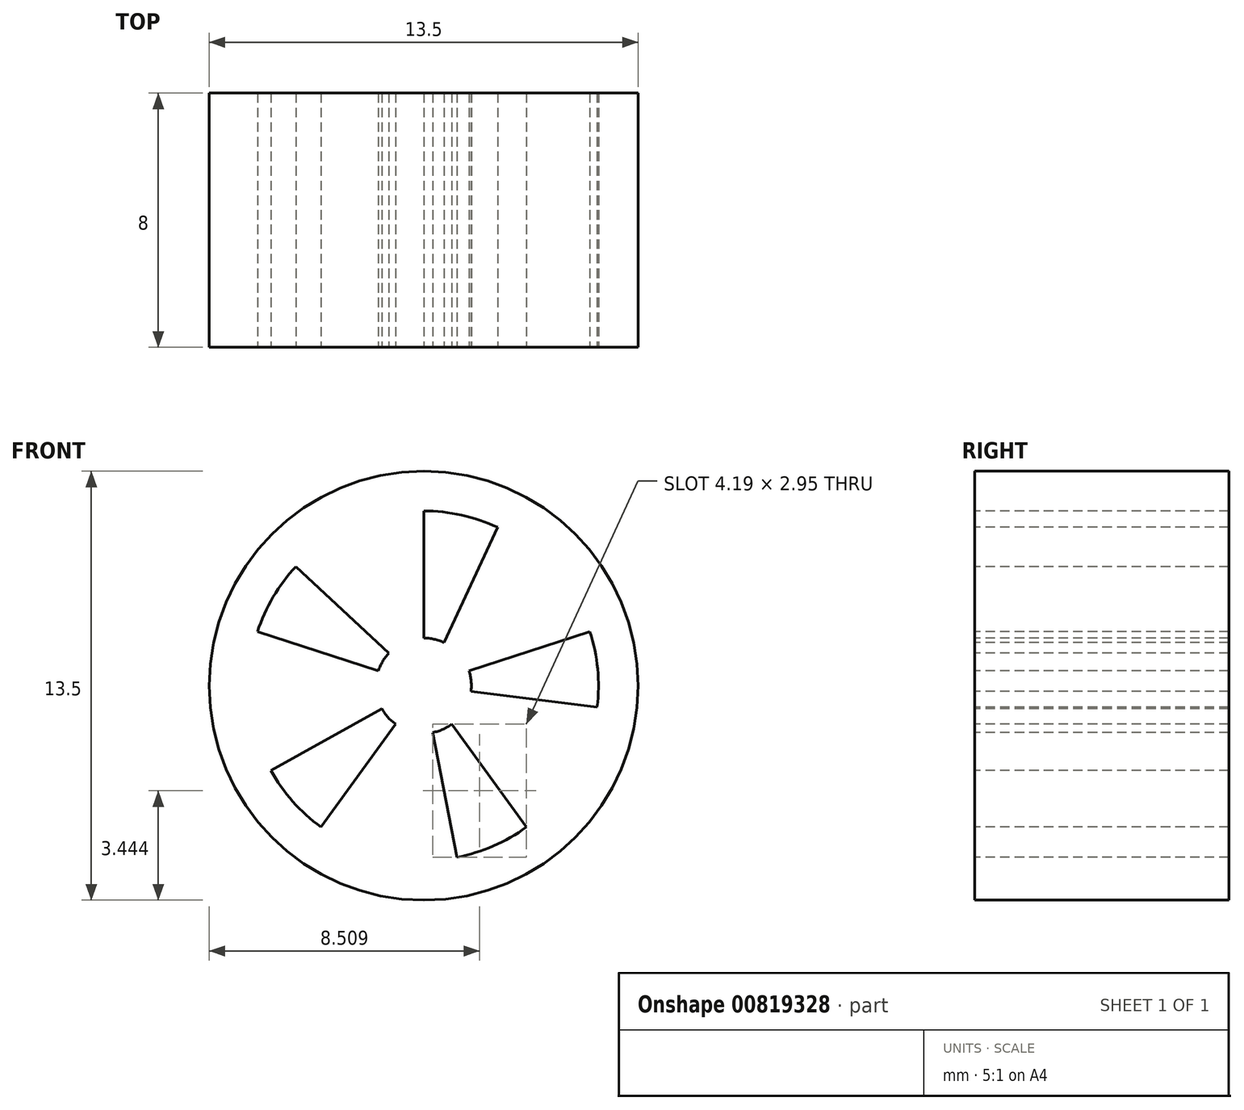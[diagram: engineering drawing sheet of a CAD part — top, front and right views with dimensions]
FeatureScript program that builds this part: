
annotation { "Feature Type Name" : "Feature", "Feature Type Description" : "" }
export const myFeature = defineFeature(function(context is Context, id is Id, definition is map)
    precondition{}
    {
        {
            var Q0;
            Q0=qCreatedBy(makeId("Front.planeOp"),FACE);
            var sketch = newSketch(context, id + "F0", { "sketchPlane" : qUnion([Q0])});
            skCircle(sketch, "E0", {"center": v(0, 0) * mm, "radius": 6.75 * mm});
            skSolve(sketch);
        }
        {
            var Q0;
            Q0=makeQuery(id+"F0.imprint","IMPRINT",FACE,{"disambiguationData":[TD([[makeQuery(id+"F0.imprint","IMPRINT",EDGE,{"derivedFrom":sQuery(id+"F0.wireOp",EDGE,"E0")}),1.0]])]});
            var Q1;
            Q1=sQuery(id+"F0.wireOp",EDGE,"E0");
            extrude(context, id + "F1", {"entities" : qUnion([Q0]), "surfaceEntities" : qUnion([Q1]), "depth" : 8 * mm, "offsetDistance" : 25 * mm});
        }
        {
            var Q0;
            Q0=makeQuery(id+"F1.opExtrude","CAP_FACE",FACE,{"disambiguationData":[OSD([sQuery(id+"F0.wireOp",EDGE,"E0")])],"isStart":false});
            var sketch = newSketch(context, id + "F2", { "sketchPlane" : qUnion([Q0])});
            skCircle(sketch, "E1", {"center": v(0, 0) * mm, "radius": 1.5 * mm});
            skCircle(sketch, "E2", {"center": v(0, 0) * mm, "radius": 5.5 * mm});
            skLineSegment(sketch, "E3", {"start": v(0, 1.5) * mm, "end": v(0, 5.5) * mm});
            skLineSegment(sketch, "E4", {"start": v(0.63, 1.36) * mm, "end": v(2.32, 4.98) * mm});
            skLineSegment(sketch, "E5.1.0", {"start": v(-1.43, 0.46) * mm, "end": v(-5.23, 1.7) * mm});
            skLineSegment(sketch, "E5.1.1", {"start": v(-1.1, 1.02) * mm, "end": v(-4.02, 3.75) * mm});
            skLineSegment(sketch, "E5.2.0", {"start": v(-0.88, -1.21) * mm, "end": v(-3.23, -4.45) * mm});
            skLineSegment(sketch, "E5.2.1", {"start": v(-1.31, -0.73) * mm, "end": v(-4.81, -2.67) * mm});
            skLineSegment(sketch, "E5.3.0", {"start": v(0.88, -1.21) * mm, "end": v(3.23, -4.45) * mm});
            skLineSegment(sketch, "E5.3.1", {"start": v(0.29, -1.47) * mm, "end": v(1.05, -5.4) * mm});
            skLineSegment(sketch, "E5.4.0", {"start": v(1.43, 0.46) * mm, "end": v(5.23, 1.7) * mm});
            skLineSegment(sketch, "E5.4.1", {"start": v(1.49, -0.18) * mm, "end": v(5.46, -0.67) * mm});
            skSolve(sketch);
        }
        {
            var Q0;
            {var subQ0=sQuery(id+"F2.wireOp",EDGE,"E5.1.1");var subQ1=sQuery(id+"F2.wireOp",EDGE,"E1");var subQ2=makeQuery(id+"F2.imprint","INTERSECT",VERTEX,{"derivedFrom":[subQ1,subQ0]});Q0=makeQuery(id+"F2.imprint","IMPRINT",FACE,{"disambiguationData":[TD([[makeQuery(id+"F2.imprint","IMPRINT",EDGE,{"disambiguationData":[TD([[subQ2,-1.0]])],"derivedFrom":subQ1}),-1.0]])]});}
            var Q1;
            {var subQ0=sQuery(id+"F2.wireOp",EDGE,"E4");var subQ1=sQuery(id+"F2.wireOp",EDGE,"E1");var subQ2=makeQuery(id+"F2.imprint","INTERSECT",VERTEX,{"derivedFrom":[subQ1,subQ0]});Q1=makeQuery(id+"F2.imprint","IMPRINT",FACE,{"disambiguationData":[TD([[makeQuery(id+"F2.imprint","IMPRINT",EDGE,{"disambiguationData":[TD([[subQ2,-1.0]])],"derivedFrom":subQ1}),-1.0]])]});}
            var Q2;
            {var subQ0=sQuery(id+"F2.wireOp",EDGE,"E5.4.0");var subQ1=sQuery(id+"F2.wireOp",EDGE,"E1");var subQ2=makeQuery(id+"F2.imprint","INTERSECT",VERTEX,{"derivedFrom":[subQ1,subQ0]});Q2=makeQuery(id+"F2.imprint","IMPRINT",FACE,{"disambiguationData":[TD([[makeQuery(id+"F2.imprint","IMPRINT",EDGE,{"disambiguationData":[TD([[subQ2,1.0]])],"derivedFrom":subQ1}),-1.0]])]});}
            var Q3;
            {var subQ0=sQuery(id+"F2.wireOp",EDGE,"E5.3.1");var subQ1=sQuery(id+"F2.wireOp",EDGE,"E1");var subQ2=makeQuery(id+"F2.imprint","INTERSECT",VERTEX,{"derivedFrom":[subQ1,subQ0]});Q3=makeQuery(id+"F2.imprint","IMPRINT",FACE,{"disambiguationData":[TD([[makeQuery(id+"F2.imprint","IMPRINT",EDGE,{"disambiguationData":[TD([[subQ2,-1.0]])],"derivedFrom":subQ1}),-1.0]])]});}
            var Q4;
            {var subQ0=sQuery(id+"F2.wireOp",EDGE,"E5.2.1");var subQ1=sQuery(id+"F2.wireOp",EDGE,"E1");var subQ2=makeQuery(id+"F2.imprint","INTERSECT",VERTEX,{"derivedFrom":[subQ1,subQ0]});Q4=makeQuery(id+"F2.imprint","IMPRINT",FACE,{"disambiguationData":[TD([[makeQuery(id+"F2.imprint","IMPRINT",EDGE,{"disambiguationData":[TD([[subQ2,-1.0]])],"derivedFrom":subQ1}),-1.0]])]});}
            extrude(context, id + "F3", {"entities" : qUnion([Q0, Q1, Q2, Q3, Q4]), "operationType" : NewBodyOperationType.REMOVE, "endBound" : BoundingType.THROUGH_ALL, "oppositeDirection" : true, "depth" : 25 * mm, "offsetDistance" : 25 * mm});
        }
    });
